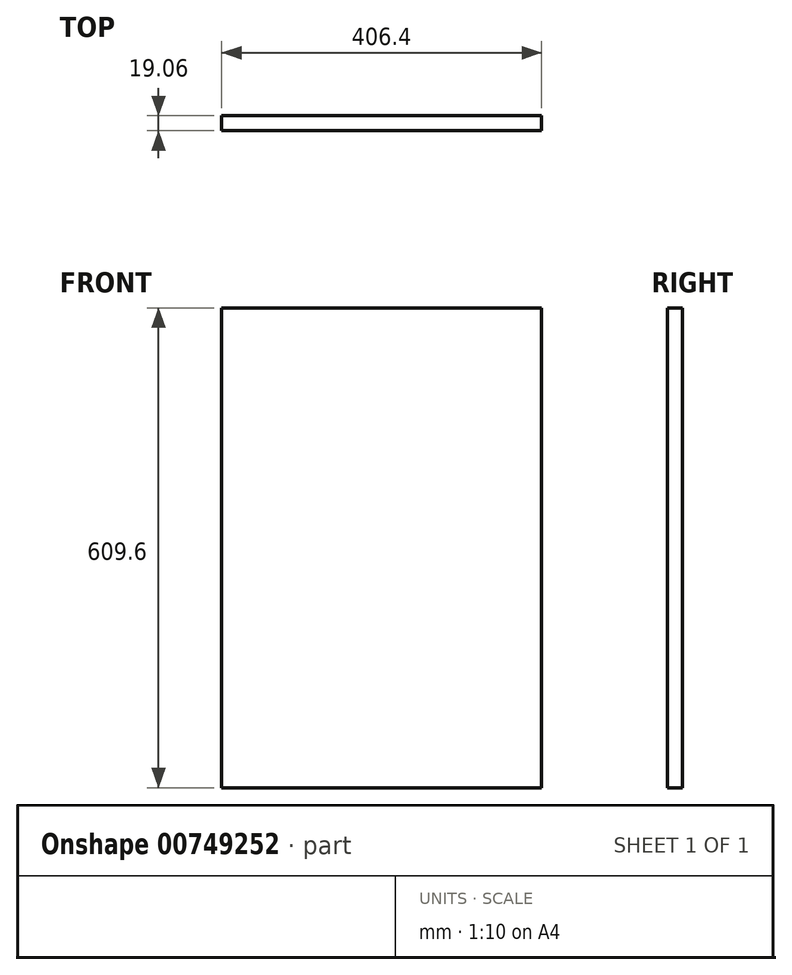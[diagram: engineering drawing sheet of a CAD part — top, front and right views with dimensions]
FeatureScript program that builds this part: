
annotation { "Feature Type Name" : "Feature", "Feature Type Description" : "" }
export const myFeature = defineFeature(function(context is Context, id is Id, definition is map)
    precondition{}
    {
        {
            var Q0;
            Q0=qCreatedBy(makeId("Top.planeOp"),FACE);
            var sketch = newSketch(context, id + "F0", { "sketchPlane" : qUnion([Q0])});
            skLineSegment(sketch, "E0.bottom", {"start": v(203.2, 9.53) * mm, "end": v(-203.2, 9.53) * mm});
            skLineSegment(sketch, "E0.top", {"start": v(203.2, -9.53) * mm, "end": v(-203.2, -9.53) * mm});
            skLineSegment(sketch, "E0.left", {"start": v(203.2, 9.53) * mm, "end": v(203.2, -9.53) * mm});
            skLineSegment(sketch, "E0.right", {"start": v(-203.2, 9.53) * mm, "end": v(-203.2, -9.53) * mm});
            skPoint(sketch, "E0.middle", {"position": v(0, 0) * mm});
            skSolve(sketch);
        }
        {
            var Q0;
            Q0=qSketchRegion(id+"F0",true);
            extrude(context, id + "F1", {"entities" : qUnion([Q0]), "depth" : 609.6 * mm, "offsetDistance" : 25.4 * mm});
        }
    });
